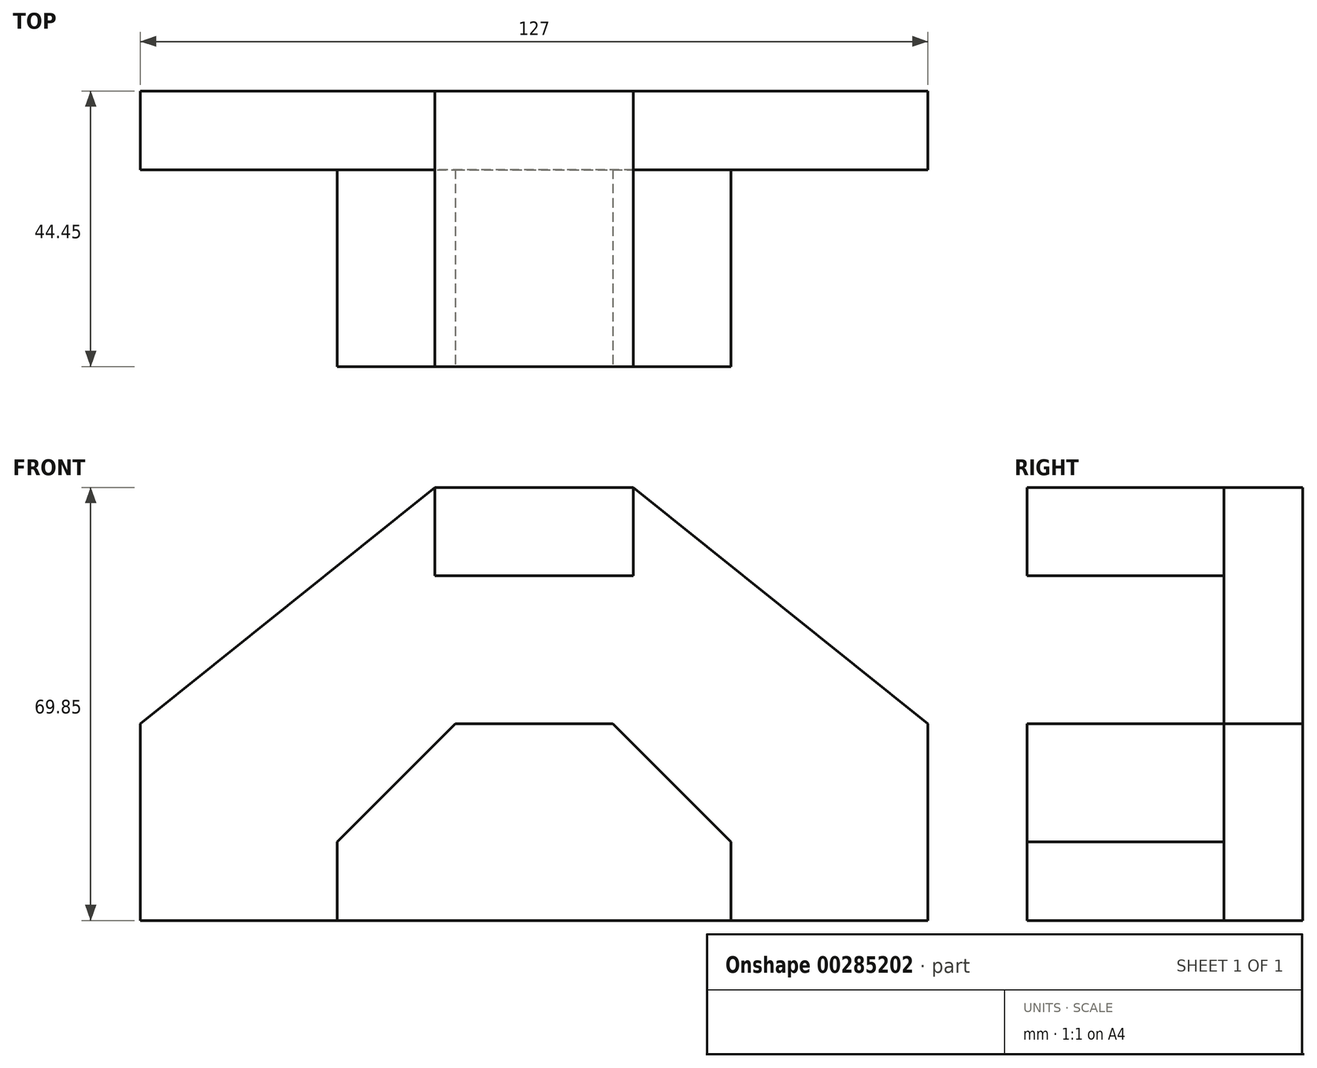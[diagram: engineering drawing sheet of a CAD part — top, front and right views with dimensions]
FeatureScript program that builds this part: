
annotation { "Feature Type Name" : "Feature", "Feature Type Description" : "" }
export const myFeature = defineFeature(function(context is Context, id is Id, definition is map)
    precondition{}
    {
        {
            var Q0;
            Q0=qCreatedBy(makeId("Front.planeOp"),FACE);
            var sketch = newSketch(context, id + "F0", { "sketchPlane" : qUnion([Q0])});
            skLineSegment(sketch, "E0", {"start": v(-62.2, -20.92) * mm, "end": v(64.8, -20.92) * mm});
            skLineSegment(sketch, "E1", {"start": v(-62.2, -20.92) * mm, "end": v(-62.2, 48.93) * mm});
            skLineSegment(sketch, "E2", {"start": v(-62.2, 48.93) * mm, "end": v(64.8, 48.93) * mm});
            skLineSegment(sketch, "E3", {"start": v(64.8, 48.93) * mm, "end": v(64.8, -20.92) * mm});
            skSolve(sketch);
        }
        {
            var Q0;
            Q0 = qSketchRegion(id + "F0", true);
            extrude(context, id + "F1", {"entities" : qUnion([Q0]), "depth" : 44.45 * mm});
        }
        {
            var Q0;
            Q0=makeQuery(id+"F1.opExtrude","CAP_FACE",FACE,{"disambiguationData":[OSD([sQuery(id+"F0.wireOp",EDGE,"E0"),sQuery(id+"F0.wireOp",EDGE,"E1"),sQuery(id+"F0.wireOp",EDGE,"E2"),sQuery(id+"F0.wireOp",EDGE,"E3")])],"isStart":false});
            var sketch = newSketch(context, id + "F2", { "sketchPlane" : qUnion([Q0])});
            skLineSegment(sketch, "E4", {"start": v(64.8, -20.92) * mm, "end": v(64.8, 10.83) * mm});
            skLineSegment(sketch, "E5", {"start": v(-62.2, -20.92) * mm, "end": v(-62.2, 10.83) * mm});
            skLineSegment(sketch, "E6", {"start": v(-62.2, 48.93) * mm, "end": v(-14.7, 48.93) * mm});
            skLineSegment(sketch, "E7", {"start": v(64.8, 48.93) * mm, "end": v(17.3, 48.93) * mm});
            skLineSegment(sketch, "E8", {"start": v(-62.2, 10.83) * mm, "end": v(-14.7, 48.93) * mm});
            skLineSegment(sketch, "E9", {"start": v(17.3, 48.93) * mm, "end": v(64.8, 10.83) * mm});
            skSolve(sketch);
        }
        {
            var Q0;
            Q0 = qSketchRegion(id + "F2", true);
            var Q1;
            {var subQ0=sQuery(id+"F2.wireOp",EDGE,"E7");Q1=makeQuery(id+"F2.imprint","IMPRINT",FACE,{"disambiguationData":[TD([[makeQuery(id+"F2.imprint","IMPRINT",EDGE,{"derivedFrom":subQ0}),-1.0]])]});}
            var Q2;
            {var subQ0=sQuery(id+"F2.wireOp",EDGE,"E6");Q2=makeQuery(id+"F2.imprint","IMPRINT",FACE,{"disambiguationData":[TD([[makeQuery(id+"F2.imprint","IMPRINT",EDGE,{"derivedFrom":subQ0}),-1.0]])]});}
            extrude(context, id + "F3", {"entities" : qUnion([Q0, Q1, Q2]), "operationType" : NewBodyOperationType.REMOVE, "oppositeDirection" : true, "depth" : 44.45 * mm});
        }
        {
            var Q0;
            Q0=makeQuery(id+"F1.opExtrude","CAP_FACE",FACE,{"disambiguationData":[OSD([sQuery(id+"F0.wireOp",EDGE,"E0"),sQuery(id+"F0.wireOp",EDGE,"E1"),sQuery(id+"F0.wireOp",EDGE,"E2"),sQuery(id+"F0.wireOp",EDGE,"E3")])],"isStart":false});
            var sketch = newSketch(context, id + "F4", { "sketchPlane" : qUnion([Q0])});
            skLineSegment(sketch, "E10", {"start": v(17.3, 48.93) * mm, "end": v(17.3, 34.7) * mm});
            skLineSegment(sketch, "E11", {"start": v(17.3, 34.7) * mm, "end": v(-14.7, 34.7) * mm});
            skLineSegment(sketch, "E12", {"start": v(-14.7, 34.7) * mm, "end": v(-14.7, 48.93) * mm});
            skLineSegment(sketch, "E13", {"start": v(64.8, -20.92) * mm, "end": v(33.06, -20.92) * mm});
            skLineSegment(sketch, "E14", {"start": v(-62.2, -20.92) * mm, "end": v(-30.44, -20.92) * mm});
            skLineSegment(sketch, "E15", {"start": v(-30.44, -20.92) * mm, "end": v(-30.44, -8.22) * mm});
            skLineSegment(sketch, "E16", {"start": v(33.06, -20.92) * mm, "end": v(33.06, -8.22) * mm});
            skLineSegment(sketch, "E17", {"start": v(-11.4, 10.83) * mm, "end": v(14, 10.83) * mm});
            skLineSegment(sketch, "E18", {"start": v(-30.44, -8.22) * mm, "end": v(-11.4, 10.83) * mm});
            skLineSegment(sketch, "E19", {"start": v(14, 10.83) * mm, "end": v(33.06, -8.22) * mm});
            skSolve(sketch);
        }
        {
            var Q0;
            Q0=makeQuery(id+"F4.imprint","IMPRINT",FACE,{"disambiguationData":[TD([[makeQuery(id+"F4.imprint","IMPRINT",EDGE,{"derivedFrom":sQuery(id+"F4.wireOp",EDGE,"E10")}),1.0]])]});
            extrude(context, id + "F5", {"entities" : qUnion([Q0]), "operationType" : NewBodyOperationType.REMOVE, "oppositeDirection" : true, "depth" : 31.75 * mm});
        }
    });
